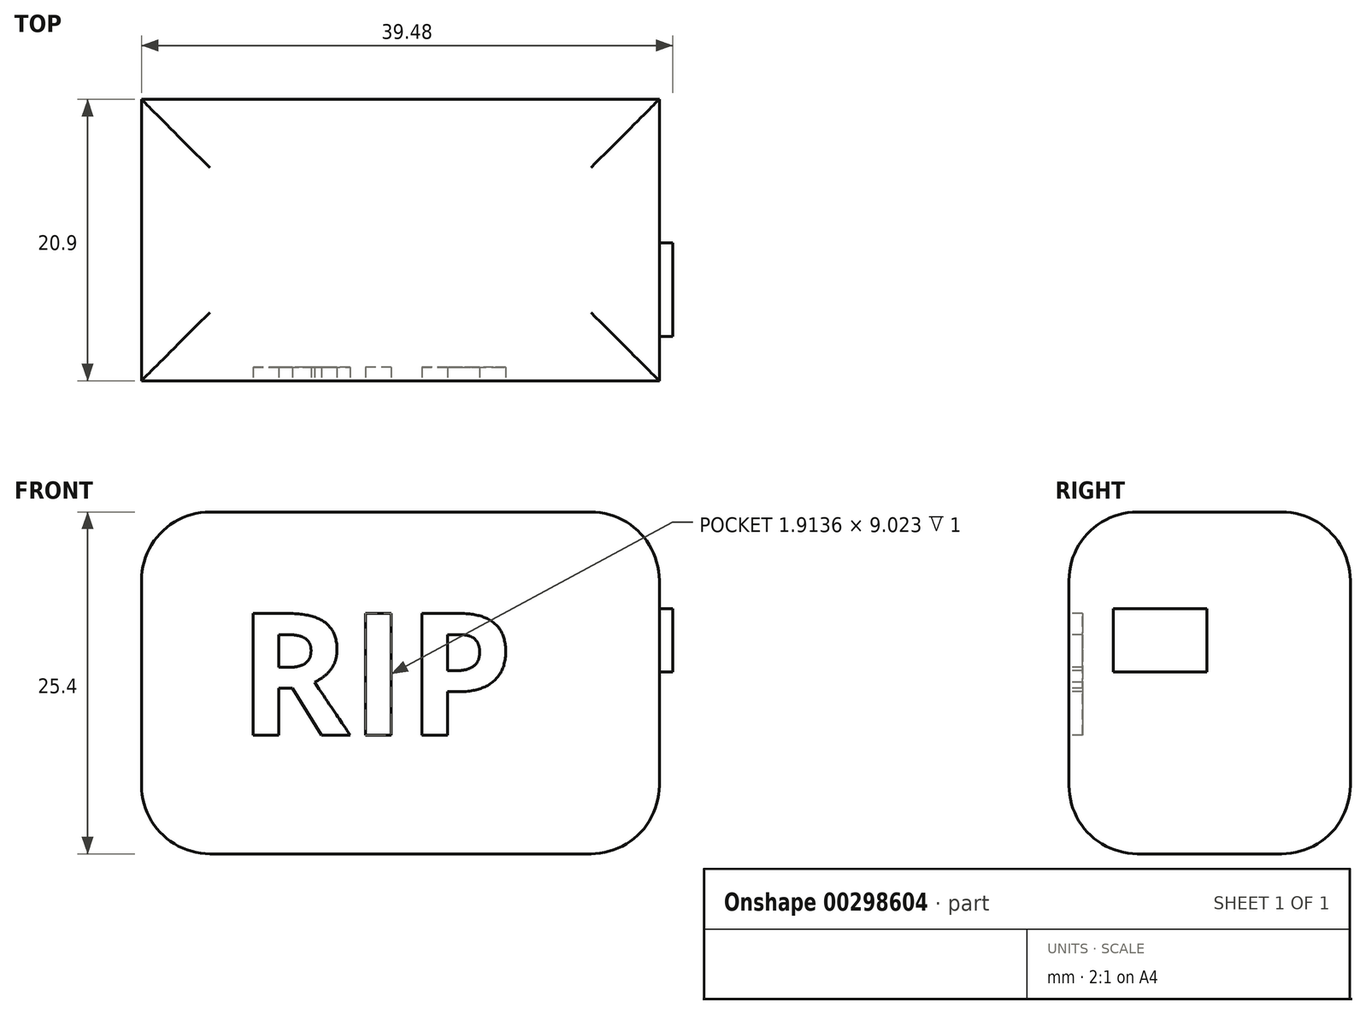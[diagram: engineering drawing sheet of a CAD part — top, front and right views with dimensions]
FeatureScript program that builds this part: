
annotation { "Feature Type Name" : "Feature", "Feature Type Description" : "" }
export const myFeature = defineFeature(function(context is Context, id is Id, definition is map)
    precondition{}
    {
        {
            var Q0;
            Q0=qCreatedBy(makeId("Top.planeOp"),FACE);
            var sketch = newSketch(context, id + "F0", { "sketchPlane" : qUnion([Q0])});
            skLineSegment(sketch, "E0.bottom", {"start": v(-62.16, 19.52) * mm, "end": v(-23.68, 19.52) * mm});
            skLineSegment(sketch, "E0.top", {"start": v(-62.16, 40.42) * mm, "end": v(-23.68, 40.42) * mm});
            skLineSegment(sketch, "E0.left", {"start": v(-62.16, 19.52) * mm, "end": v(-62.16, 40.42) * mm});
            skLineSegment(sketch, "E0.right", {"start": v(-23.68, 19.52) * mm, "end": v(-23.68, 40.42) * mm});
            skSolve(sketch);
        }
        {
            var Q0;
            Q0 = qSketchRegion(id + "F0", true);
            var Q1;
            Q1=makeQuery(id+"F0.imprint","IMPRINT",FACE,{"disambiguationData":[TD([[makeQuery(id+"F0.imprint","IMPRINT",EDGE,{"derivedFrom":sQuery(id+"F0.wireOp",EDGE,"E0.bottom")}),1.0]])]});
            extrude(context, id + "F1", {"entities" : qUnion([Q0, Q1]), "depth" : 25.4 * mm});
        }
        {
            var Q0;
            Q0=makeQuery(id+"F1.opExtrude","CAP_EDGE",EDGE,{"disambiguationData":[OSD([sQuery(id+"F0.wireOp",EDGE,"E0.bottom")])],"isStart":false});
            var Q1;
            Q1=makeQuery(id+"F1.opExtrude","CAP_EDGE",EDGE,{"disambiguationData":[OSD([sQuery(id+"F0.wireOp",EDGE,"E0.top")])],"isStart":false});
            var Q2;
            Q2=makeQuery(id+"F1.opExtrude","CAP_EDGE",EDGE,{"disambiguationData":[OSD([sQuery(id+"F0.wireOp",EDGE,"E0.left")])],"isStart":true});
            var Q3;
            Q3=makeQuery(id+"F1.opExtrude","CAP_EDGE",EDGE,{"disambiguationData":[OSD([sQuery(id+"F0.wireOp",EDGE,"E0.right")])],"isStart":true});
            var Q4;
            Q4=makeQuery(id+"F1.opExtrude","CAP_EDGE",EDGE,{"disambiguationData":[OSD([sQuery(id+"F0.wireOp",EDGE,"E0.bottom")])],"isStart":true});
            var Q5;
            Q5=makeQuery(id+"F1.opExtrude","CAP_EDGE",EDGE,{"disambiguationData":[OSD([sQuery(id+"F0.wireOp",EDGE,"E0.top")])],"isStart":true});
            var Q6;
            Q6=makeQuery(id+"F1.opExtrude","CAP_EDGE",EDGE,{"disambiguationData":[OSD([sQuery(id+"F0.wireOp",EDGE,"E0.left")])],"isStart":false});
            var Q7;
            Q7=makeQuery(id+"F1.opExtrude","CAP_EDGE",EDGE,{"disambiguationData":[OSD([sQuery(id+"F0.wireOp",EDGE,"E0.right")])],"isStart":false});
            fillet(context, id + "F2", {"entities" : qUnion([Q0, Q1, Q2, Q3, Q4, Q5, Q6, Q7]), "radius" : 5.08 * mm, "tangentPropagation" : true, "allowEdgeOverflow" : false});
        }
        {
            var Q0;
            Q0=makeQuery(id+"F1.opExtrude","SWEPT_FACE",FACE,{"disambiguationData":[OSD([sQuery(id+"F0.wireOp",EDGE,"E0.bottom")])]});
            var sketch = newSketch(context, id + "F3", { "sketchPlane" : qUnion([Q0])});
            skText(sketch, "E1", { "text": "RIP", "fontName": "OpenSans-Bold.ttf"});
            const initialGuessF3  = {"E1": [-0.05499, 0.00883, 1, 0, 0.0091]};
            skSetInitialGuess(sketch, initialGuessF3);
            skSolve(sketch);
        }
        {
            var Q0;
            Q0 = qSketchRegion(id + "F3", true);
            extrude(context, id + "F4", {"entities" : qUnion([Q0]), "operationType" : NewBodyOperationType.REMOVE, "oppositeDirection" : true, "depth" : 1 * mm});
        }
        {
            var Q0;
            Q0=makeQuery(id+"F1.opExtrude","SWEPT_FACE",FACE,{"disambiguationData":[OSD([sQuery(id+"F0.wireOp",EDGE,"E0.right")])]});
            var sketch = newSketch(context, id + "F5", { "sketchPlane" : qUnion([Q0])});
            skLineSegment(sketch, "E2", {"start": v(29.76, 13.52) * mm, "end": v(29.76, 18.2) * mm});
            skLineSegment(sketch, "E3", {"start": v(29.76, 18.2) * mm, "end": v(22.81, 18.2) * mm});
            skLineSegment(sketch, "E4", {"start": v(22.81, 18.2) * mm, "end": v(22.81, 13.5) * mm});
            skLineSegment(sketch, "E5", {"start": v(22.81, 13.5) * mm, "end": v(29.76, 13.52) * mm});
            skSolve(sketch);
        }
        {
            var Q0;
            Q0=makeQuery(id+"F5.imprint","IMPRINT",FACE,{"disambiguationData":[TD([[makeQuery(id+"F5.imprint","IMPRINT",EDGE,{"derivedFrom":sQuery(id+"F5.wireOp",EDGE,"E2")}),1.0]])]});
            extrude(context, id + "F6", {"entities" : qUnion([Q0]), "operationType" : NewBodyOperationType.ADD, "depth" : 1 * mm});
        }
    });
